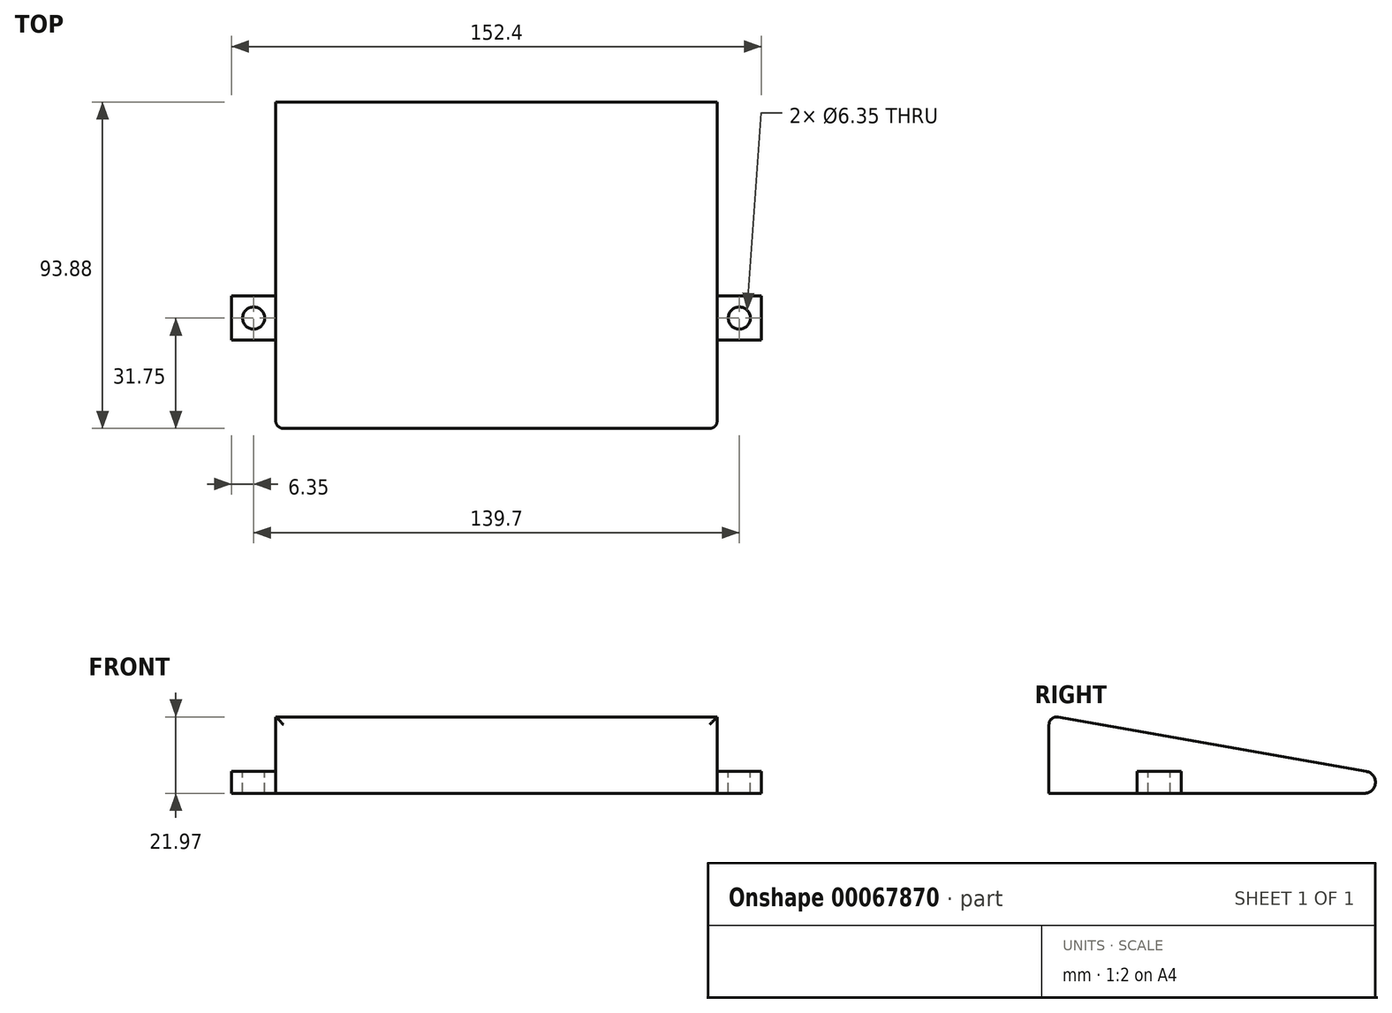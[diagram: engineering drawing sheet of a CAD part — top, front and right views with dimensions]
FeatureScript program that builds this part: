
annotation { "Feature Type Name" : "Feature", "Feature Type Description" : "" }
export const myFeature = defineFeature(function(context is Context, id is Id, definition is map)
    precondition{}
    {
        {
            var Q0;
            Q0=qCreatedBy(makeId("Right.planeOp"),FACE);
            var sketch = newSketch(context, id + "F0", { "sketchPlane" : qUnion([Q0])});
            skLineSegment(sketch, "E0.bottom", {"start": v(0, 0) * mm, "end": v(-127, 0) * mm});
            skLineSegment(sketch, "E0.top", {"start": v(0, 22.4) * mm, "end": v(-127, 22.4) * mm});
            skLineSegment(sketch, "E0.left", {"start": v(0, 0) * mm, "end": v(0, 22.4) * mm});
            skLineSegment(sketch, "E0.right", {"start": v(-127, 0) * mm, "end": v(-127, 22.4) * mm});
            skLineSegment(sketch, "E1", {"start": v(-127, 22.4) * mm, "end": v(0, 0) * mm});
            skSolve(sketch);
        }
        {
            var Q0;
            Q0=makeQuery(id+"F0.imprint","IMPRINT",FACE,{"disambiguationData":[TD([[makeQuery(id+"F0.imprint","IMPRINT",EDGE,{"derivedFrom":sQuery(id+"F0.wireOp",EDGE,"E0.bottom")}),-1.0]])]});
            extrude(context, id + "F1", {"entities" : qUnion([Q0]), "depth" : 127 * mm});
        }
        {
            var Q0;
            Q0=makeQuery(id+"F1.opExtrude","CAP_FACE",FACE,{"disambiguationData":[OSD([sQuery(id+"F0.wireOp",EDGE,"E0.bottom"),sQuery(id+"F0.wireOp",EDGE,"E0.right"),sQuery(id+"F0.wireOp",EDGE,"E1")])],"isStart":false});
            var sketch = newSketch(context, id + "F2", { "sketchPlane" : qUnion([Q0])});
            skLineSegment(sketch, "E2.bottom", {"start": v(-88.9, 0) * mm, "end": v(-101.6, 0) * mm});
            skLineSegment(sketch, "E2.left", {"start": v(-88.9, 0) * mm, "end": v(-88.9, 6.35) * mm});
            skLineSegment(sketch, "E2.right", {"start": v(-101.6, 0) * mm, "end": v(-101.6, 6.35) * mm});
            skLineSegment(sketch, "E3.bottom", {"start": v(-101.6, 6.35) * mm, "end": v(-88.9, 6.35) * mm});
            skLineSegment(sketch, "E3.top", {"start": v(-101.6, 0) * mm, "end": v(-88.9, 0) * mm});
            skLineSegment(sketch, "E3.left", {"start": v(-101.6, 6.35) * mm, "end": v(-101.6, 0) * mm});
            skLineSegment(sketch, "E3.right", {"start": v(-88.9, 6.35) * mm, "end": v(-88.9, 0) * mm});
            skSolve(sketch);
        }
        {
            var Q0;
            Q0=makeQuery(id+"F2.imprint","IMPRINT",FACE,{"disambiguationData":[TD([[makeQuery(id+"F2.imprint","IMPRINT",EDGE,{"derivedFrom":sQuery(id+"F2.wireOp",EDGE,"E3.bottom")}),-1.0]])]});
            extrude(context, id + "F3", {"entities" : qUnion([Q0]), "operationType" : NewBodyOperationType.ADD, "depth" : 12.7 * mm});
        }
        {
            var Q0;
            Q0=makeQuery(id+"F1.opExtrude","CAP_FACE",FACE,{"disambiguationData":[OSD([sQuery(id+"F0.wireOp",EDGE,"E0.bottom"),sQuery(id+"F0.wireOp",EDGE,"E0.right"),sQuery(id+"F0.wireOp",EDGE,"E1")])],"isStart":true});
            var sketch = newSketch(context, id + "F4", { "sketchPlane" : qUnion([Q0])});
            skLineSegment(sketch, "E4.bottom", {"start": v(101.6, 0) * mm, "end": v(88.9, 0) * mm});
            skLineSegment(sketch, "E4.top", {"start": v(101.6, 6.35) * mm, "end": v(88.9, 6.35) * mm});
            skLineSegment(sketch, "E4.left", {"start": v(101.6, 0) * mm, "end": v(101.6, 6.35) * mm});
            skLineSegment(sketch, "E4.right", {"start": v(88.9, 0) * mm, "end": v(88.9, 6.35) * mm});
            skSolve(sketch);
        }
        {
            var Q0;
            Q0=makeQuery(id+"F4.imprint","IMPRINT",FACE,{"disambiguationData":[TD([[makeQuery(id+"F4.imprint","IMPRINT",EDGE,{"derivedFrom":sQuery(id+"F4.wireOp",EDGE,"E4.bottom")}),1.0]])]});
            extrude(context, id + "F5", {"entities" : qUnion([Q0]), "operationType" : NewBodyOperationType.ADD, "depth" : 12.7 * mm});
        }
        {
            var Q0;
            Q0=makeQuery(id+"F5.opExtrude","SWEPT_FACE",FACE,{"disambiguationData":[OSD([sQuery(id+"F4.wireOp",EDGE,"E4.top")])]});
            var sketch = newSketch(context, id + "F6", { "sketchPlane" : qUnion([Q0])});
            skCircle(sketch, "E5", {"center": v(-6.35, -95.25) * mm, "radius": 3.18 * mm});
            skSolve(sketch);
        }
        {
            var Q0;
            Q0=makeQuery(id+"F6.imprint","IMPRINT",FACE,{"disambiguationData":[TD([[makeQuery(id+"F6.imprint","IMPRINT",EDGE,{"derivedFrom":sQuery(id+"F6.wireOp",EDGE,"E5")}),1.0]])]});
            extrude(context, id + "F7", {"entities" : qUnion([Q0]), "operationType" : NewBodyOperationType.REMOVE, "endBound" : BoundingType.THROUGH_ALL, "oppositeDirection" : true, "depth" : 25.4 * mm});
        }
        {
            var Q0;
            Q0=makeQuery(id+"F3.opExtrude","SWEPT_FACE",FACE,{"disambiguationData":[OSD([sQuery(id+"F2.wireOp",EDGE,"E3.bottom")])]});
            var sketch = newSketch(context, id + "F8", { "sketchPlane" : qUnion([Q0])});
            skCircle(sketch, "E6", {"center": v(133.35, -95.25) * mm, "radius": 3.18 * mm});
            skPoint(sketch, "E6.centerSnap0", {"position": v(127, -95.25) * mm});
            skSolve(sketch);
        }
        {
            var Q0;
            Q0=makeQuery(id+"F8.imprint","IMPRINT",FACE,{"disambiguationData":[TD([[makeQuery(id+"F8.imprint","IMPRINT",EDGE,{"derivedFrom":sQuery(id+"F8.wireOp",EDGE,"E6")}),1.0]])]});
            extrude(context, id + "F9", {"entities" : qUnion([Q0]), "operationType" : NewBodyOperationType.REMOVE, "endBound" : BoundingType.THROUGH_ALL, "oppositeDirection" : true, "depth" : 25.4 * mm});
        }
        {
            var Q0;
            Q0=makeQuery(id+"F1.opExtrude","SWEPT_EDGE",EDGE,{"disambiguationData":[OSD([sQuery(id+"F0.wireOp",EDGE,"E0.bottom"),sQuery(id+"F0.wireOp",EDGE,"E0.left"),sQuery(id+"F0.wireOp",EDGE,"E1")])]});
            fillet(context, id + "F10", {"entities" : qUnion([Q0]), "radius" : 3.17 * mm, "tangentPropagation" : true, "allowEdgeOverflow" : false});
        }
        {
            var Q0;
            Q0=makeQuery(id+"F1.opExtrude","SWEPT_EDGE",EDGE,{"disambiguationData":[OSD([sQuery(id+"F0.wireOp",EDGE,"E0.top"),sQuery(id+"F0.wireOp",EDGE,"E0.right"),sQuery(id+"F0.wireOp",EDGE,"E1")])]});
            var Q1;
            Q1=makeQuery(id+"F1.opExtrude","CAP_EDGE",EDGE,{"disambiguationData":[OSD([sQuery(id+"F0.wireOp",EDGE,"E0.right")])],"isStart":false});
            var Q2;
            Q2=makeQuery(id+"F1.opExtrude","CAP_EDGE",EDGE,{"disambiguationData":[OSD([sQuery(id+"F0.wireOp",EDGE,"E0.right")])],"isStart":true});
            fillet(context, id + "F11", {"entities" : qUnion([Q0, Q1, Q2]), "radius" : 2.22 * mm, "tangentPropagation" : true, "allowEdgeOverflow" : false});
        }
    });
